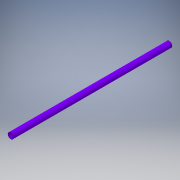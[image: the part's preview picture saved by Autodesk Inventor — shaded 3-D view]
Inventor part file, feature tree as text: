
AUTODESK INVENTOR PART (.ipt)
format: ipt  version: 2018 (Build 220112000, 112)  size: 105,984 bytes
history: native  units: in
note: dims shown in document units (in); Inventor stores cm internally (conversion verified against a paired STEP export)
features: extrude x1, sketch x1
ambient origin geometry x8: Origin, YZ Plane, XZ Plane, XY Plane, X Axis, Y Axis, Z Axis, Center Point
bodies: Solid1 (feature_tree)
feature tree (2):
  extrude  "Extrusion1"  Depth=36.0in
  sketch  "Sketch1"  dims[d0=1.315in d1=1.0in d2=36.0in d3=0.0in]
